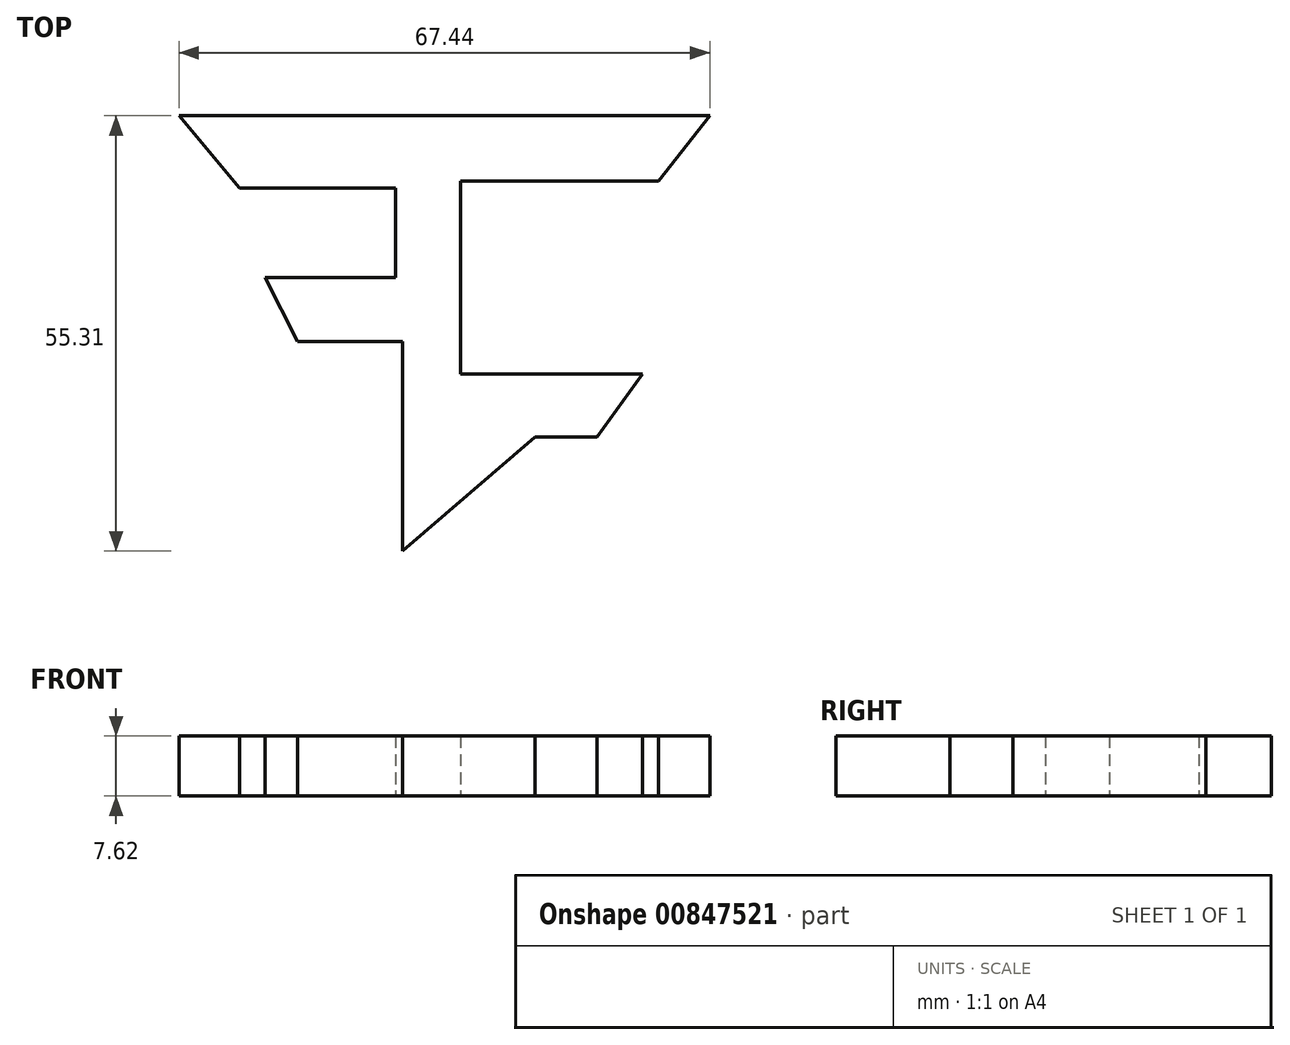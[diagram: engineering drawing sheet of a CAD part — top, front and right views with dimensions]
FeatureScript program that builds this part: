
annotation { "Feature Type Name" : "Feature", "Feature Type Description" : "" }
export const myFeature = defineFeature(function(context is Context, id is Id, definition is map)
    precondition{}
    {
        {
            var Q0;
            Q0=qCreatedBy(makeId("Top.planeOp"),FACE);
            var sketch = newSketch(context, id + "F0", { "sketchPlane" : qUnion([Q0])});
            skLineSegment(sketch, "E0", {"start": v(34.9, 32.83) * mm, "end": v(28.4, 24.55) * mm});
            skLineSegment(sketch, "E1", {"start": v(28.4, 24.55) * mm, "end": v(3.25, 24.55) * mm});
            skLineSegment(sketch, "E2", {"start": v(3.25, 24.55) * mm, "end": v(3.25, 0) * mm});
            skLineSegment(sketch, "E3", {"start": v(20.56, -7.99) * mm, "end": v(12.72, -7.99) * mm});
            skLineSegment(sketch, "E4", {"start": v(34.9, 32.83) * mm, "end": v(-32.54, 32.83) * mm});
            skLineSegment(sketch, "E5", {"start": v(-32.54, 32.83) * mm, "end": v(-24.85, 23.66) * mm});
            skLineSegment(sketch, "E6", {"start": v(-24.85, 23.66) * mm, "end": v(-5.03, 23.66) * mm});
            skLineSegment(sketch, "E7", {"start": v(-5.03, 23.66) * mm, "end": v(-5.03, 12.28) * mm});
            skPoint(sketch, "E7.endSnap0", {"position": v(3.25, 12.28) * mm});
            skLineSegment(sketch, "E8", {"start": v(-5.03, 12.28) * mm, "end": v(-21.6, 12.28) * mm});
            skLineSegment(sketch, "E9", {"start": v(-21.6, 12.28) * mm, "end": v(-17.45, 4.14) * mm});
            skLineSegment(sketch, "E10", {"start": v(-17.45, 4.14) * mm, "end": v(-4.14, 4.14) * mm});
            skLineSegment(sketch, "E11", {"start": v(-4.14, 4.14) * mm, "end": v(-4.14, -22.48) * mm});
            skLineSegment(sketch, "E12", {"start": v(-4.14, -22.48) * mm, "end": v(12.72, -7.99) * mm});
            skPoint(sketch, "E13.start.orphan", {"position": v(34.9, 0) * mm});
            skLineSegment(sketch, "E14", {"start": v(3.25, 0) * mm, "end": v(26.32, 0) * mm});
            skLineSegment(sketch, "E15", {"start": v(26.32, 0) * mm, "end": v(20.56, -7.99) * mm});
            skPoint(sketch, "E16.orphan", {"position": v(28.4, -7.99) * mm});
            skSolve(sketch);
        }
        {
            var Q0;
            Q0=makeQuery(id+"F0.imprint","IMPRINT",FACE,{"disambiguationData":[TD([[makeQuery(id+"F0.imprint","IMPRINT",EDGE,{"derivedFrom":sQuery(id+"F0.wireOp",EDGE,"E0")}),-1.0]])]});
            extrude(context, id + "F1", {"entities" : qUnion([Q0]), "depth" : 7.62 * mm, "offsetDistance" : 25.4 * mm});
        }
    });
